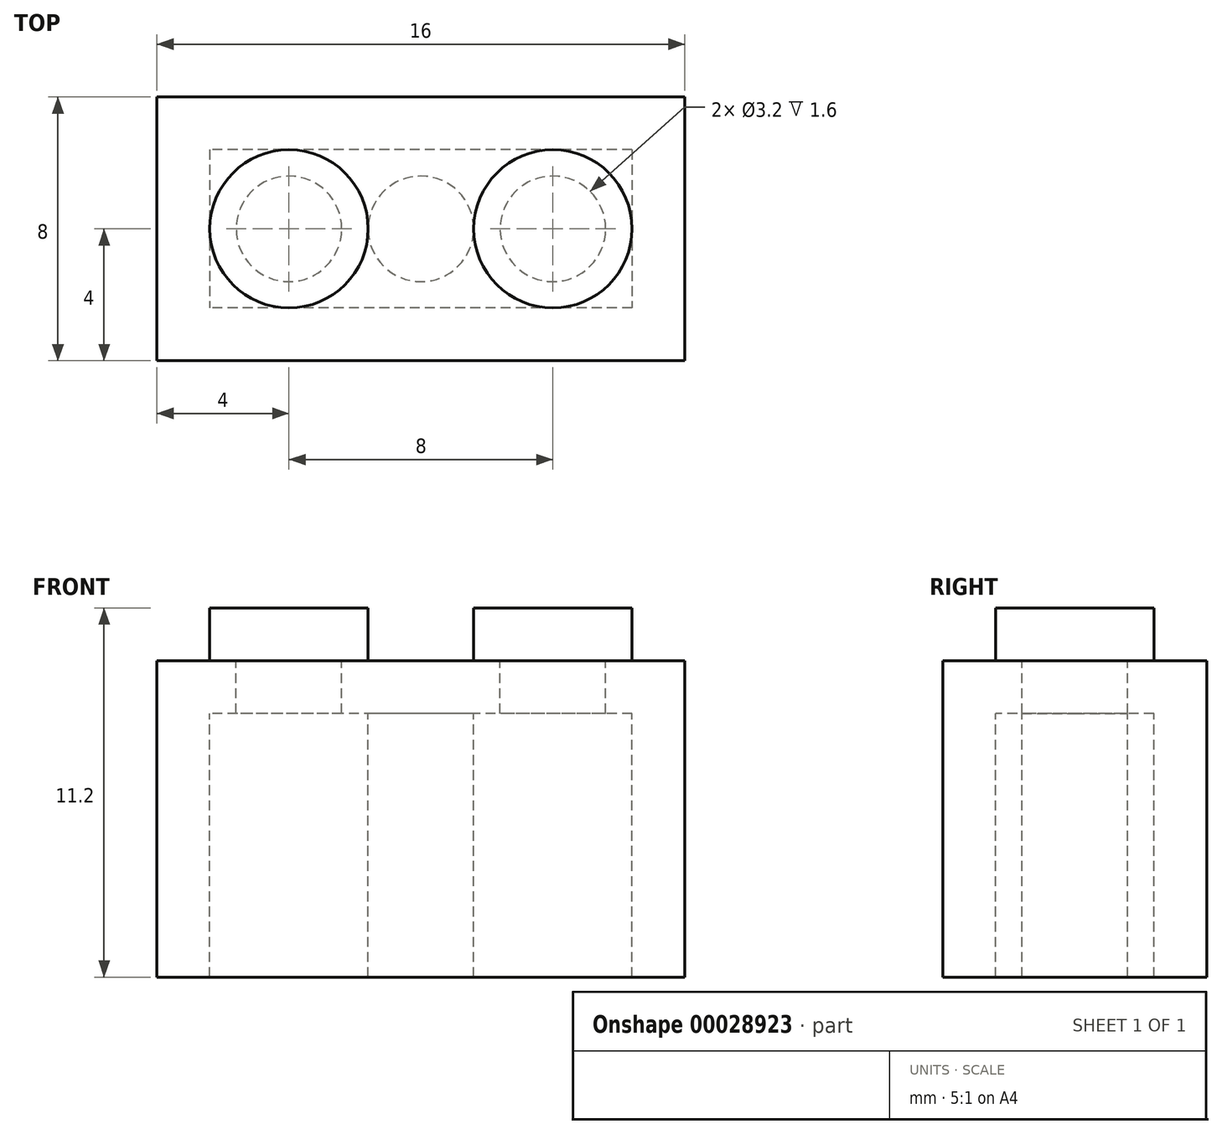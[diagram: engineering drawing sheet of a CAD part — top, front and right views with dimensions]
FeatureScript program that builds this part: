
annotation { "Feature Type Name" : "Feature", "Feature Type Description" : "" }
export const myFeature = defineFeature(function(context is Context, id is Id, definition is map)
    precondition{}
    {
        {
            var Q0;
            Q0=qCreatedBy(makeId("Top.planeOp"),FACE);
            var sketch = newSketch(context, id + "F0", { "sketchPlane" : qUnion([Q0])});
            skLineSegment(sketch, "E0.rect.bottom", {"start": v(8, 4) * mm, "end": v(-8, 4) * mm});
            skLineSegment(sketch, "E0.rect.top", {"start": v(8, -4) * mm, "end": v(-8, -4) * mm});
            skLineSegment(sketch, "E0.rect.left", {"start": v(8, 4) * mm, "end": v(8, -4) * mm});
            skLineSegment(sketch, "E0.rect.right", {"start": v(-8, 4) * mm, "end": v(-8, -4) * mm});
            skPoint(sketch, "E0.rect.middle", {"position": v(0, 0) * mm});
            skLineSegment(sketch, "E1.0", {"start": v(6.4, 2.4) * mm, "end": v(6.4, -2.4) * mm});
            skLineSegment(sketch, "E1.1", {"start": v(6.4, 2.4) * mm, "end": v(-6.4, 2.4) * mm});
            skLineSegment(sketch, "E1.2", {"start": v(-6.4, 2.4) * mm, "end": v(-6.4, -2.4) * mm});
            skLineSegment(sketch, "E1.3", {"start": v(6.4, -2.4) * mm, "end": v(-6.4, -2.4) * mm});
            skCircle(sketch, "E2", {"center": v(-4, 0) * mm, "radius": 2.4 * mm});
            skCircle(sketch, "E3", {"center": v(4, 0) * mm, "radius": 2.4 * mm});
            skCircle(sketch, "E4", {"center": v(4, 0) * mm, "radius": 1.6 * mm});
            skCircle(sketch, "E5", {"center": v(-4, 0) * mm, "radius": 1.6 * mm});
            skCircle(sketch, "E6", {"center": v(0, 0) * mm, "radius": 1.6 * mm});
            skSolve(sketch);
        }
        {
            var Q0;
            Q0=makeQuery(id+"F0.imprint","IMPRINT",FACE,{"disambiguationData":[TD([[makeQuery(id+"F0.imprint","IMPRINT",EDGE,{"derivedFrom":sQuery(id+"F0.wireOp",EDGE,"E5")}),-1.0]])]});
            var Q1;
            Q1=makeQuery(id+"F0.imprint","IMPRINT",FACE,{"disambiguationData":[TD([[makeQuery(id+"F0.imprint","IMPRINT",EDGE,{"derivedFrom":sQuery(id+"F0.wireOp",EDGE,"E5")}),1.0]])]});
            var Q2;
            Q2=makeQuery(id+"F0.imprint","IMPRINT",FACE,{"disambiguationData":[TD([[makeQuery(id+"F0.imprint","IMPRINT",EDGE,{"derivedFrom":sQuery(id+"F0.wireOp",EDGE,"E4")}),1.0]])]});
            var Q3;
            Q3=makeQuery(id+"F0.imprint","IMPRINT",FACE,{"disambiguationData":[TD([[makeQuery(id+"F0.imprint","IMPRINT",EDGE,{"derivedFrom":sQuery(id+"F0.wireOp",EDGE,"E4")}),-1.0]])]});
            extrude(context, id + "F1", {"entities" : qUnion([Q0, Q1, Q2, Q3]), "depth" : 1.6 * mm});
        }
        {
            var Q0;
            Q0=makeQuery(id+"F1.opExtrude","CAP_FACE",FACE,{"disambiguationData":[OSD([sQuery(id+"F0.wireOp",EDGE,"E2")])],"isStart":false});
            var Q1;
            {var subQ1=sQuery(id+"F0.wireOp",EDGE,"E3");var subQ5=sQuery(id+"F0.wireOp",EDGE,"E1.3");var subQ6=makeQuery(id+"F0.imprint","INTERSECT",VERTEX,{"derivedFrom":[subQ5,subQ1]});Q1=makeQuery(id+"F0.imprint","IMPRINT",FACE,{"disambiguationData":[TD([[makeQuery(id+"F0.imprint","IMPRINT",EDGE,{"disambiguationData":[TD([[subQ6,-1.0]])],"derivedFrom":subQ5}),-1.0]])]});}
            var Q2;
            {var subQ1=sQuery(id+"F0.wireOp",EDGE,"E3");var subQ5=sQuery(id+"F0.wireOp",EDGE,"E1.1");var subQ6=makeQuery(id+"F0.imprint","INTERSECT",VERTEX,{"derivedFrom":[subQ5,subQ1]});Q2=makeQuery(id+"F0.imprint","IMPRINT",FACE,{"disambiguationData":[TD([[makeQuery(id+"F0.imprint","IMPRINT",EDGE,{"disambiguationData":[TD([[subQ6,-1.0]])],"derivedFrom":subQ5}),1.0]])]});}
            var Q3;
            {var subQ0=sQuery(id+"F0.wireOp",EDGE,"E1.2");var subQ3=sQuery(id+"F0.wireOp",EDGE,"E1.1");var subQ4=makeQuery(id+"F0.imprint","INTERSECT",VERTEX,{"derivedFrom":[subQ3,subQ0]});Q3=makeQuery(id+"F0.imprint","IMPRINT",FACE,{"disambiguationData":[TD([[makeQuery(id+"F0.imprint","IMPRINT",EDGE,{"disambiguationData":[TD([[subQ4,1.0]])],"derivedFrom":subQ3}),1.0]])]});}
            var Q4;
            {var subQ1=sQuery(id+"F0.wireOp",EDGE,"E1.3");var subQ3=sQuery(id+"F0.wireOp",EDGE,"E1.2");var subQ5=makeQuery(id+"F0.imprint","INTERSECT",VERTEX,{"derivedFrom":[subQ3,subQ1]});Q4=makeQuery(id+"F0.imprint","IMPRINT",FACE,{"disambiguationData":[TD([[makeQuery(id+"F0.imprint","IMPRINT",EDGE,{"disambiguationData":[TD([[subQ5,1.0]])],"derivedFrom":subQ3}),1.0]])]});}
            var Q5;
            {var subQ1=sQuery(id+"F0.wireOp",EDGE,"E1.3");var subQ3=sQuery(id+"F0.wireOp",EDGE,"E1.0");var subQ5=makeQuery(id+"F0.imprint","INTERSECT",VERTEX,{"derivedFrom":[subQ3,subQ1]});Q5=makeQuery(id+"F0.imprint","IMPRINT",FACE,{"disambiguationData":[TD([[makeQuery(id+"F0.imprint","IMPRINT",EDGE,{"disambiguationData":[TD([[subQ5,1.0]])],"derivedFrom":subQ3}),-1.0]])]});}
            var Q6;
            Q6=makeQuery(id+"F1.opExtrude","CAP_FACE",FACE,{"disambiguationData":[OSD([sQuery(id+"F0.wireOp",EDGE,"E3")])],"isStart":false});
            var Q7;
            {var subQ1=sQuery(id+"F0.wireOp",EDGE,"E1.1");var subQ3=sQuery(id+"F0.wireOp",EDGE,"E1.0");var subQ5=makeQuery(id+"F0.imprint","INTERSECT",VERTEX,{"derivedFrom":[subQ3,subQ1]});Q7=makeQuery(id+"F0.imprint","IMPRINT",FACE,{"disambiguationData":[TD([[makeQuery(id+"F0.imprint","IMPRINT",EDGE,{"disambiguationData":[TD([[subQ5,-1.0]])],"derivedFrom":subQ3}),-1.0]])]});}
            var Q8;
            {var subQ0=sQuery(id+"F0.wireOp",EDGE,"E6");var subQ2=makeQuery(id+"F0.imprint","INTERSECT",VERTEX,{"derivedFrom":[sQuery(id+"F0.wireOp",EDGE,"E2"),subQ0]});Q8=makeQuery(id+"F0.imprint","IMPRINT",FACE,{"disambiguationData":[TD([[makeQuery(id+"F0.imprint","IMPRINT",EDGE,{"disambiguationData":[TD([[subQ2,1.0]])],"derivedFrom":subQ0}),1.0]])]});}
            var Q9;
            Q9=makeQuery(id+"F0.imprint","IMPRINT",FACE,{"disambiguationData":[TD([[makeQuery(id+"F0.imprint","IMPRINT",EDGE,{"derivedFrom":sQuery(id+"F0.wireOp",EDGE,"E5")}),-1.0]])]});
            var Q10;
            Q10=makeQuery(id+"F0.imprint","IMPRINT",FACE,{"disambiguationData":[TD([[makeQuery(id+"F0.imprint","IMPRINT",EDGE,{"derivedFrom":sQuery(id+"F0.wireOp",EDGE,"E4")}),-1.0]])]});
            extrude(context, id + "F2", {"entities" : qUnion([Q0, Q1, Q2, Q3, Q4, Q5, Q6, Q7, Q8, Q9, Q10]), "operationType" : NewBodyOperationType.ADD, "oppositeDirection" : true, "depth" : 1.6 * mm});
        }
        {
            var Q0;
            Q0=makeQuery(id+"F0.imprint","IMPRINT",FACE,{"disambiguationData":[TD([[makeQuery(id+"F0.imprint","IMPRINT",EDGE,{"derivedFrom":sQuery(id+"F0.wireOp",EDGE,"E0.rect.bottom")}),1.0]])]});
            var Q1;
            {var subQ0=sQuery(id+"F0.wireOp",EDGE,"E6");var subQ2=makeQuery(id+"F0.imprint","INTERSECT",VERTEX,{"derivedFrom":[sQuery(id+"F0.wireOp",EDGE,"E2"),subQ0]});Q1=makeQuery(id+"F0.imprint","IMPRINT",FACE,{"disambiguationData":[TD([[makeQuery(id+"F0.imprint","IMPRINT",EDGE,{"disambiguationData":[TD([[subQ2,1.0]])],"derivedFrom":subQ0}),1.0]])]});}
            extrude(context, id + "F3", {"entities" : qUnion([Q0, Q1]), "operationType" : NewBodyOperationType.ADD, "oppositeDirection" : true, "depth" : 9.6 * mm});
        }
    });
